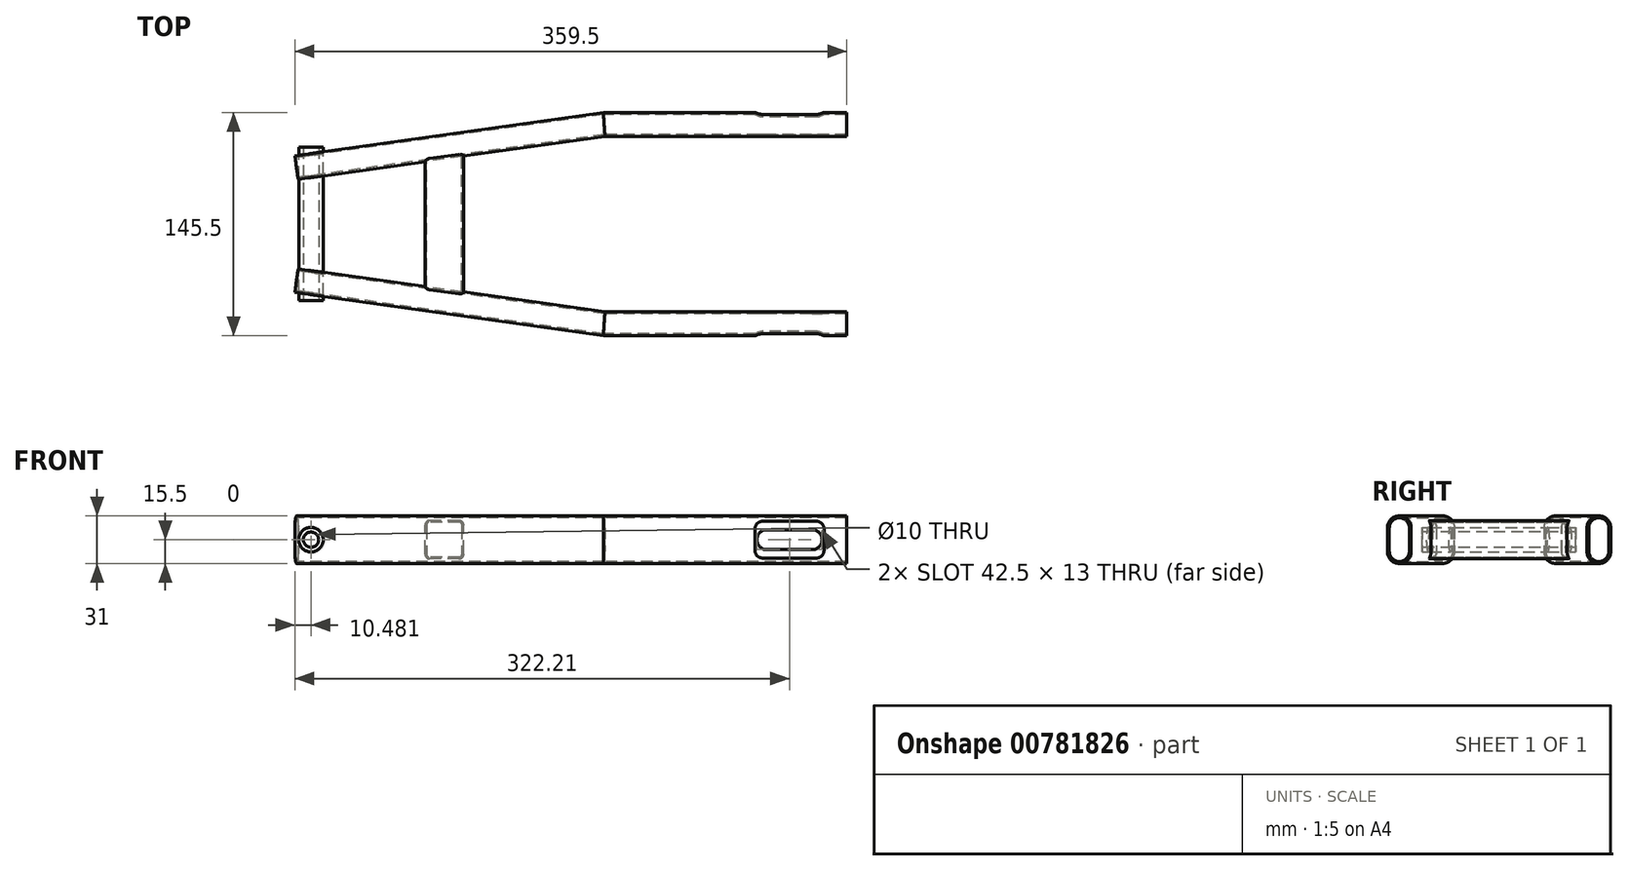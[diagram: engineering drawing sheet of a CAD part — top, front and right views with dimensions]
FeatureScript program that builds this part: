
annotation { "Feature Type Name" : "Feature", "Feature Type Description" : "" }
export const myFeature = defineFeature(function(context is Context, id is Id, definition is map)
    precondition{}
    {
        {
            var Q0;
            Q0=qCreatedBy(makeId("Top.planeOp"),FACE);
            var sketch = newSketch(context, id + "F0", { "sketchPlane" : qUnion([Q0])});
            skLineSegment(sketch, "E0", {"start": v(0, 65) * mm, "end": v(-158.03, 65) * mm});
            skLineSegment(sketch, "E1", {"start": v(-158.03, 65) * mm, "end": v(-358.42, 36.84) * mm});
            skSolve(sketch);
        }
        {
            var Q0;
            Q0=qCreatedBy(makeId("Right.planeOp"),FACE);
            var sketch = newSketch(context, id + "F1", { "sketchPlane" : qUnion([Q0])});
            skLineSegment(sketch, "E2.left", {"start": v(57.25, 7.75) * mm, "end": v(57.25, -7.75) * mm});
            skLineSegment(sketch, "E2.right", {"start": v(72.75, 7.75) * mm, "end": v(72.75, -7.75) * mm});
            skPoint(sketch, "E2.middle", {"position": v(65, 0) * mm});
            skArc(sketch, "E3", {"start": v(57.25, 7.75) * mm, "mid": v(65, 15.5) * mm, "end": v(72.75, 7.75) * mm});
            skArc(sketch, "E4", {"start": v(57.25, -7.75) * mm, "mid": v(65, -15.5) * mm, "end": v(72.75, -7.75) * mm});
            skArc(sketch, "E5.0", {"start": v(58.45, 7.75) * mm, "mid": v(65, 14.3) * mm, "end": v(71.55, 7.75) * mm});
            skLineSegment(sketch, "E6.0", {"start": v(58.45, 7.75) * mm, "end": v(58.45, -7.75) * mm});
            skLineSegment(sketch, "E7.0", {"start": v(71.55, 7.75) * mm, "end": v(71.55, -7.75) * mm});
            skArc(sketch, "E8.0", {"start": v(58.45, -7.75) * mm, "mid": v(65, -14.3) * mm, "end": v(71.55, -7.75) * mm});
            skSolve(sketch);
        }
        {
            var Q0;
            Q0=makeQuery(id+"F1.imprint","IMPRINT",FACE,{"disambiguationData":[TD([[makeQuery(id+"F1.imprint","IMPRINT",EDGE,{"derivedFrom":sQuery(id+"F1.wireOp",EDGE,"E2.left")}),1.0]])]});
            var Q1;
            Q1=sQuery(id+"F0.wireOp",EDGE,"E0");
            var Q2;
            Q2=sQuery(id+"F0.wireOp",EDGE,"E1");
            sweep(context, id + "F2", {"profiles" : qUnion([Q0]), "path" : qUnion([Q1, Q2])});
        }
        {
            var Q0;
            Q0=makeQuery(id+"F2.opSweep","SWEPT_BODY",BODY,{"disambiguationData":[OSD([sQuery(id+"F0.wireOp",EDGE,"E1"),sQuery(id+"F1.wireOp",EDGE,"E5.0"),sQuery(id+"F1.wireOp",EDGE,"E6.0"),sQuery(id+"F1.wireOp",EDGE,"E7.0"),sQuery(id+"F1.wireOp",EDGE,"E8.0")])]});
            var Q1;
            Q1=qCreatedBy(makeId("Front.planeOp"),FACE);
            mirror(context, id + "F3", {"entities" : qUnion([Q0]), "mirrorPlane" : qUnion([Q1])});
        }
        {
            var Q0;
            Q0=qCreatedBy(makeId("Front.planeOp"),FACE);
            var sketch = newSketch(context, id + "F4", { "sketchPlane" : qUnion([Q0])});
            skCircle(sketch, "E9", {"center": v(-349.02, 0) * mm, "radius": 8 * mm});
            skSolve(sketch);
        }
        {
            var Q0;
            Q0 = qSketchRegion(id + "F4", true);
            extrude(context, id + "F5", {"entities" : qUnion([Q0]), "operationType" : NewBodyOperationType.ADD, "endBound" : BoundingType.SYMMETRIC, "depth" : 100 * mm, "offsetDistance" : 25 * mm});
        }
        {
            var Q0;
            Q0=makeQuery(id+"F5.opExtrude","CAP_FACE",FACE,{"disambiguationData":[OSD([sQuery(id+"F4.wireOp",EDGE,"E9")])],"isStart":false});
            var sketch = newSketch(context, id + "F6", { "sketchPlane" : qUnion([Q0])});
            skCircle(sketch, "E10", {"center": v(-349.02, 0) * mm, "radius": 5 * mm});
            skSolve(sketch);
        }
        {
            var Q0;
            Q0=makeQuery(id+"F6.imprint","IMPRINT",FACE,{"disambiguationData":[TD([[makeQuery(id+"F6.imprint","IMPRINT",EDGE,{"derivedFrom":sQuery(id+"F6.wireOp",EDGE,"E10")}),1.0]])]});
            extrude(context, id + "F7", {"entities" : qUnion([Q0]), "operationType" : NewBodyOperationType.REMOVE, "endBound" : BoundingType.THROUGH_ALL, "oppositeDirection" : true, "depth" : 25 * mm, "offsetDistance" : 25 * mm});
        }
        {
            var Q0;
            Q0=qCreatedBy(makeId("Front.planeOp"),FACE);
            var sketch = newSketch(context, id + "F8", { "sketchPlane" : qUnion([Q0])});
            skLineSegment(sketch, "E11.bottom", {"start": v(-22.54, -6.5) * mm, "end": v(-52.04, -6.5) * mm});
            skLineSegment(sketch, "E11.top", {"start": v(-22.54, 6.5) * mm, "end": v(-52.04, 6.5) * mm});
            skPoint(sketch, "E11.middle", {"position": v(-37.3, 0) * mm});
            skArc(sketch, "E12", {"start": v(-52.04, -6.5) * mm, "mid": v(-58.54, 0) * mm, "end": v(-52.04, 6.5) * mm});
            skArc(sketch, "E13", {"start": v(-22.54, -6.5) * mm, "mid": v(-16.04, 0) * mm, "end": v(-22.54, 6.5) * mm});
            skSolve(sketch);
        }
        {
            var Q0;
            Q0=makeQuery(id+"F8.imprint","IMPRINT",FACE,{"disambiguationData":[TD([[makeQuery(id+"F8.imprint","IMPRINT",EDGE,{"derivedFrom":sQuery(id+"F8.wireOp",EDGE,"E11.bottom")}),-1.0]])]});
            extrude(context, id + "F9", {"entities" : qUnion([Q0]), "operationType" : NewBodyOperationType.REMOVE, "endBound" : BoundingType.SYMMETRIC, "oppositeDirection" : true, "depth" : 125 * mm, "offsetDistance" : 25 * mm});
        }
        {
            var Q0;
            Q0=qCreatedBy(makeId("Front.planeOp"),FACE);
            var sketch = newSketch(context, id + "F10", { "sketchPlane" : qUnion([Q0])});
            skLineSegment(sketch, "E14.bottom", {"start": v(-19.76, -12) * mm, "end": v(-54.76, -12) * mm});
            skLineSegment(sketch, "E14.top", {"start": v(-19.76, 12) * mm, "end": v(-54.76, 12) * mm});
            skLineSegment(sketch, "E14.left", {"start": v(-14.76, -7) * mm, "end": v(-14.76, 7) * mm});
            skLineSegment(sketch, "E14.right", {"start": v(-59.76, -7) * mm, "end": v(-59.76, 7) * mm});
            skPoint(sketch, "E14.middle", {"position": v(-37.26, 0) * mm});
            skPoint(sketch, "E15.visualSharp", {"position": v(-59.76, 12) * mm});
            skArc(sketch, "E15.filletArc", {"start": v(-54.76, 12) * mm, "mid": v(-58.3, 10.54) * mm, "end": v(-59.76, 7) * mm});
            skPoint(sketch, "E16.visualSharp", {"position": v(-59.76, -12) * mm});
            skArc(sketch, "E16.filletArc", {"start": v(-59.76, -7) * mm, "mid": v(-58.3, -10.54) * mm, "end": v(-54.76, -12) * mm});
            skPoint(sketch, "E17.visualSharp", {"position": v(-14.76, -12) * mm});
            skArc(sketch, "E17.filletArc", {"start": v(-19.76, -12) * mm, "mid": v(-16.22, -10.54) * mm, "end": v(-14.76, -7) * mm});
            skPoint(sketch, "E18.visualSharp", {"position": v(-14.76, 12) * mm});
            skArc(sketch, "E18.filletArc", {"start": v(-14.76, 7) * mm, "mid": v(-16.22, 10.54) * mm, "end": v(-19.76, 12) * mm});
            skSolve(sketch);
        }
        {
            var Q0;
            Q0=makeQuery(id+"F2.opSweep","SWEPT_FACE",FACE,{"disambiguationData":[OSD([sQuery(id+"F0.wireOp",EDGE,"E0"),sQuery(id+"F1.wireOp",EDGE,"E2.right")])]});
            var sketch = newSketch(context, id + "F11", { "sketchPlane" : qUnion([Q0])});
            skArc(sketch, "E19.0.0", {"start": v(14.76, 7) * mm, "mid": v(16.22, 10.54) * mm, "end": v(19.76, 12) * mm});
            skLineSegment(sketch, "E19.0.1", {"start": v(19.76, 12) * mm, "end": v(54.76, 12) * mm});
            skArc(sketch, "E19.0.2", {"start": v(54.76, 12) * mm, "mid": v(58.3, 10.54) * mm, "end": v(59.76, 7) * mm});
            skLineSegment(sketch, "E19.0.3", {"start": v(59.76, 7) * mm, "end": v(59.76, -7) * mm});
            skArc(sketch, "E19.0.4", {"start": v(59.76, -7) * mm, "mid": v(58.3, -10.54) * mm, "end": v(54.76, -12) * mm});
            skLineSegment(sketch, "E19.0.5", {"start": v(54.76, -12) * mm, "end": v(19.76, -12) * mm});
            skArc(sketch, "E19.0.6", {"start": v(19.76, -12) * mm, "mid": v(16.22, -10.54) * mm, "end": v(14.76, -7) * mm});
            skLineSegment(sketch, "E19.0.7", {"start": v(14.76, -7) * mm, "end": v(14.76, 7) * mm});
            skSolve(sketch);
        }
        {
            var Q0;
            Q0 = qSketchRegion(id + "F11", true);
            extrude(context, id + "F12", {"entities" : qUnion([Q0]), "operationType" : NewBodyOperationType.REMOVE, "oppositeDirection" : true, "depth" : 4 * mm, "offsetDistance" : 25 * mm});
        }
        {
            var Q0;
            Q0=makeQuery(id+"F3.opPattern","COPY",FACE,{"derivedFrom":makeQuery(id+"F2.opSweep","SWEPT_FACE",FACE,{"disambiguationData":[OSD([sQuery(id+"F0.wireOp",EDGE,"E0"),sQuery(id+"F1.wireOp",EDGE,"E2.right")])]}),"instanceName":"1"});
            var sketch = newSketch(context, id + "F13", { "sketchPlane" : qUnion([Q0])});
            skArc(sketch, "E20.0.0", {"start": v(-14.76, 7) * mm, "mid": v(-16.22, 10.54) * mm, "end": v(-19.76, 12) * mm});
            skLineSegment(sketch, "E20.0.1", {"start": v(-19.76, 12) * mm, "end": v(-54.76, 12) * mm});
            skArc(sketch, "E20.0.2", {"start": v(-54.76, 12) * mm, "mid": v(-58.3, 10.54) * mm, "end": v(-59.76, 7) * mm});
            skLineSegment(sketch, "E20.0.3", {"start": v(-59.76, 7) * mm, "end": v(-59.76, -7) * mm});
            skArc(sketch, "E20.0.4", {"start": v(-59.76, -7) * mm, "mid": v(-58.3, -10.54) * mm, "end": v(-54.76, -12) * mm});
            skLineSegment(sketch, "E20.0.5", {"start": v(-54.76, -12) * mm, "end": v(-19.76, -12) * mm});
            skArc(sketch, "E20.0.6", {"start": v(-19.76, -12) * mm, "mid": v(-16.22, -10.54) * mm, "end": v(-14.76, -7) * mm});
            skLineSegment(sketch, "E20.0.7", {"start": v(-14.76, -7) * mm, "end": v(-14.76, 7) * mm});
            skSolve(sketch);
        }
        {
            var Q0;
            Q0 = qSketchRegion(id + "F13", true);
            extrude(context, id + "F14", {"entities" : qUnion([Q0]), "operationType" : NewBodyOperationType.REMOVE, "oppositeDirection" : true, "depth" : 4 * mm, "offsetDistance" : 25 * mm});
        }
        {
            var Q0;
            Q0=qCreatedBy(makeId("Front.planeOp"),FACE);
            var sketch = newSketch(context, id + "F15", { "sketchPlane" : qUnion([Q0])});
            skLineSegment(sketch, "E21.bottom", {"start": v(-271.69, -12.5) * mm, "end": v(-252.69, -12.5) * mm});
            skLineSegment(sketch, "E21.top", {"start": v(-271.69, 12.5) * mm, "end": v(-252.69, 12.5) * mm});
            skLineSegment(sketch, "E21.left", {"start": v(-274.69, -9.5) * mm, "end": v(-274.69, 9.5) * mm});
            skLineSegment(sketch, "E21.right", {"start": v(-249.69, -9.5) * mm, "end": v(-249.69, 9.5) * mm});
            skPoint(sketch, "E21.middle", {"position": v(-262.19, 0) * mm});
            skLineSegment(sketch, "E22.bottom", {"start": v(-272.19, -11.4) * mm, "end": v(-252.19, -11.4) * mm});
            skLineSegment(sketch, "E22.top", {"start": v(-272.19, 11.4) * mm, "end": v(-252.19, 11.4) * mm});
            skLineSegment(sketch, "E22.left", {"start": v(-273.59, -10) * mm, "end": v(-273.59, 10) * mm});
            skLineSegment(sketch, "E22.right", {"start": v(-250.79, -10) * mm, "end": v(-250.79, 10) * mm});
            skPoint(sketch, "E23.visualSharp", {"position": v(-274.69, -12.5) * mm});
            skArc(sketch, "E23.filletArc", {"start": v(-274.69, -9.5) * mm, "mid": v(-273.81, -11.62) * mm, "end": v(-271.69, -12.5) * mm});
            skPoint(sketch, "E24.visualSharp", {"position": v(-249.69, -12.5) * mm});
            skArc(sketch, "E24.filletArc", {"start": v(-252.69, -12.5) * mm, "mid": v(-250.57, -11.62) * mm, "end": v(-249.69, -9.5) * mm});
            skPoint(sketch, "E25.visualSharp", {"position": v(-249.69, 12.5) * mm});
            skArc(sketch, "E25.filletArc", {"start": v(-249.69, 9.5) * mm, "mid": v(-250.57, 11.62) * mm, "end": v(-252.69, 12.5) * mm});
            skPoint(sketch, "E26.visualSharp", {"position": v(-274.69, 12.5) * mm});
            skArc(sketch, "E26.filletArc", {"start": v(-271.69, 12.5) * mm, "mid": v(-273.81, 11.62) * mm, "end": v(-274.69, 9.5) * mm});
            skPoint(sketch, "E27.visualSharp", {"position": v(-273.59, 11.4) * mm});
            skArc(sketch, "E27.filletArc", {"start": v(-272.19, 11.4) * mm, "mid": v(-273.18, 10.99) * mm, "end": v(-273.59, 10) * mm});
            skPoint(sketch, "E28.visualSharp", {"position": v(-273.59, -11.4) * mm});
            skArc(sketch, "E28.filletArc", {"start": v(-273.59, -10) * mm, "mid": v(-273.18, -10.99) * mm, "end": v(-272.19, -11.4) * mm});
            skPoint(sketch, "E29.visualSharp", {"position": v(-250.79, -11.4) * mm});
            skArc(sketch, "E29.filletArc", {"start": v(-252.19, -11.4) * mm, "mid": v(-251.2, -10.99) * mm, "end": v(-250.79, -10) * mm});
            skPoint(sketch, "E30.visualSharp", {"position": v(-250.79, 11.4) * mm});
            skArc(sketch, "E30.filletArc", {"start": v(-250.79, 10) * mm, "mid": v(-251.2, 10.99) * mm, "end": v(-252.19, 11.4) * mm});
            skSolve(sketch);
        }
        {
            var Q0;
            Q0 = qSketchRegion(id + "F15", true);
            extrude(context, id + "F16", {"entities" : qUnion([Q0]), "operationType" : NewBodyOperationType.ADD, "endBound" : BoundingType.UP_TO_NEXT, "depth" : 25 * mm, "offsetDistance" : 25 * mm, "hasSecondDirection" : true, "secondDirectionBound" : SecondDirectionBoundingType.UP_TO_NEXT, "secondDirectionOppositeDirection" : true, "secondDirectionDepth" : 25 * mm});
        }
    });
